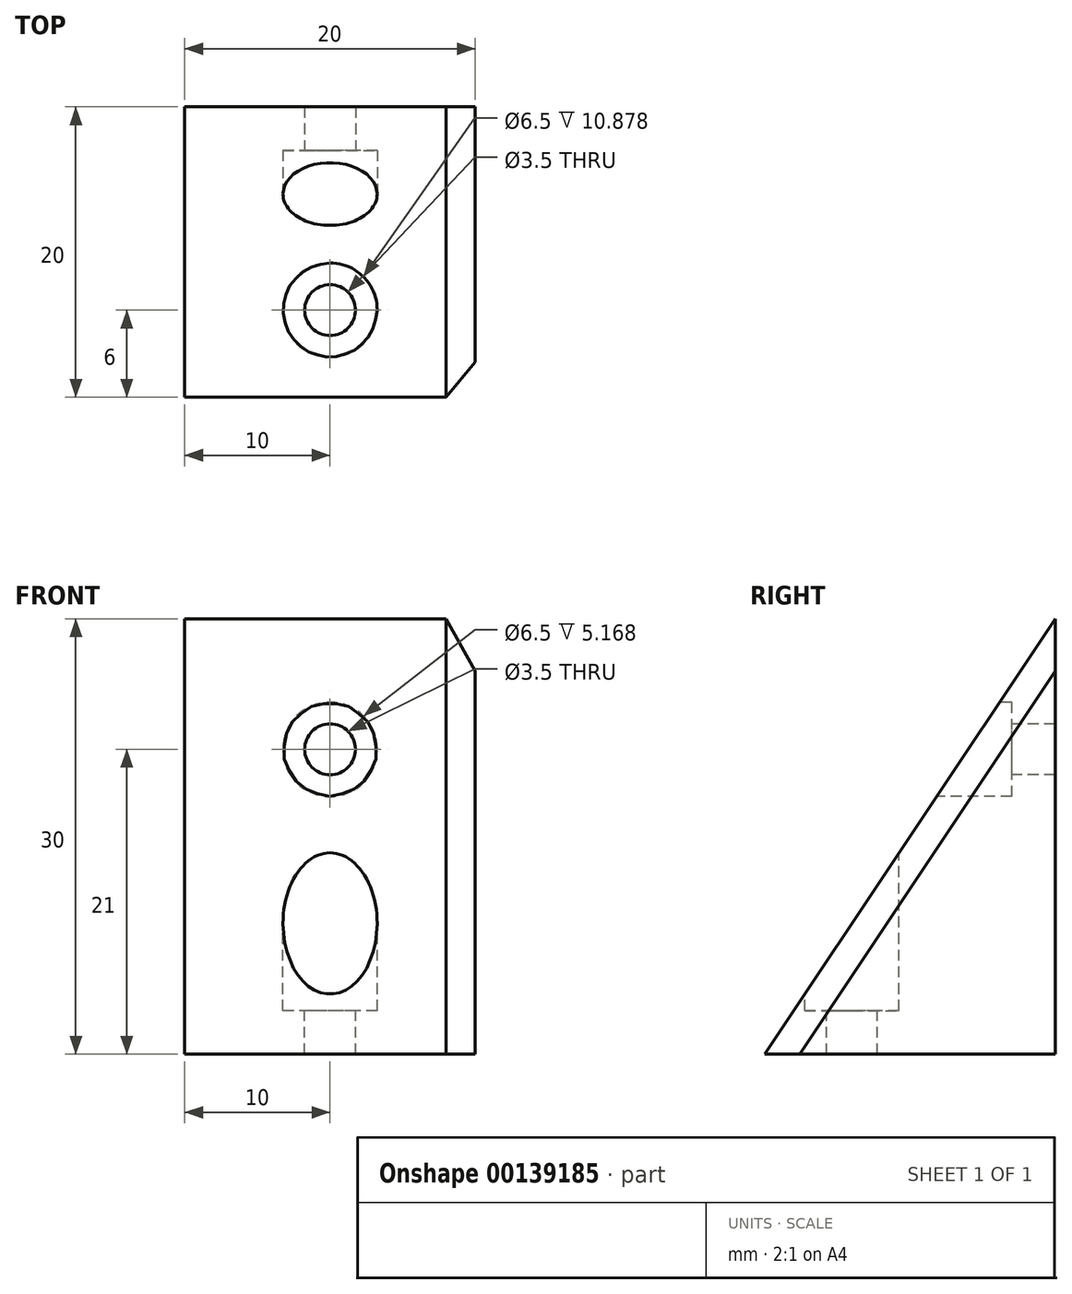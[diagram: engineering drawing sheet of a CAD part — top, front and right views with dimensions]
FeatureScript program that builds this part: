
annotation { "Feature Type Name" : "Feature", "Feature Type Description" : "" }
export const myFeature = defineFeature(function(context is Context, id is Id, definition is map)
    precondition{}
    {
        {
            var Q0;
            Q0=qCreatedBy(makeId("Front.planeOp"),FACE);
            var sketch = newSketch(context, id + "F0", { "sketchPlane" : qUnion([Q0])});
            skLineSegment(sketch, "E0.bottom", {"start": v(0, 0) * mm, "end": v(20, 0) * mm});
            skLineSegment(sketch, "E0.top", {"start": v(0, 30) * mm, "end": v(20, 30) * mm});
            skLineSegment(sketch, "E0.left", {"start": v(0, 0) * mm, "end": v(0, 30) * mm});
            skLineSegment(sketch, "E0.right", {"start": v(20, 0) * mm, "end": v(20, 30) * mm});
            skSolve(sketch);
        }
        {
            var Q0;
            Q0=makeQuery(id+"F0.imprint","IMPRINT",FACE,{"disambiguationData":[TD([[makeQuery(id+"F0.imprint","IMPRINT",EDGE,{"derivedFrom":sQuery(id+"F0.wireOp",EDGE,"E0.bottom")}),1.0]])]});
            extrude(context, id + "F1", {"entities" : qUnion([Q0]), "depth" : 20 * mm});
        }
        {
            var Q0;
            Q0=makeQuery(id+"F1.opExtrude","CAP_FACE",FACE,{"disambiguationData":[OSD([sQuery(id+"F0.wireOp",EDGE,"E0.bottom"),sQuery(id+"F0.wireOp",EDGE,"E0.top"),sQuery(id+"F0.wireOp",EDGE,"E0.left"),sQuery(id+"F0.wireOp",EDGE,"E0.right")])],"isStart":false});
            var sketch = newSketch(context, id + "F2", { "sketchPlane" : qUnion([Q0])});
            skCircle(sketch, "E1", {"center": v(10, 21) * mm, "radius": 3.25 * mm});
            skPoint(sketch, "E1.centerSnap0", {"position": v(10, 30) * mm});
            skCircle(sketch, "E2", {"center": v(10, 21) * mm, "radius": 1.75 * mm});
            skSolve(sketch);
        }
        {
            var Q0;
            Q0=makeQuery(id+"F2.imprint","IMPRINT",FACE,{"disambiguationData":[TD([[makeQuery(id+"F2.imprint","IMPRINT",EDGE,{"derivedFrom":sQuery(id+"F2.wireOp",EDGE,"E1")}),1.0]])]});
            extrude(context, id + "F3", {"entities" : qUnion([Q0]), "operationType" : NewBodyOperationType.REMOVE, "oppositeDirection" : true, "depth" : 17 * mm});
        }
        {
            var Q0;
            Q0=makeQuery(id+"F3.boolean.opBoolean","SPLIT",FACE,{"disambiguationData":[TD([makeQuery(id+"F3.opExtrude","SWEPT_FACE",FACE,{"disambiguationData":[OSD([sQuery(id+"F2.wireOp",EDGE,"E2")])]})])],"derivedFrom":makeQuery(id+"F1.opExtrude","CAP_FACE",FACE,{"disambiguationData":[OSD([sQuery(id+"F0.wireOp",EDGE,"E0.bottom"),sQuery(id+"F0.wireOp",EDGE,"E0.top"),sQuery(id+"F0.wireOp",EDGE,"E0.left"),sQuery(id+"F0.wireOp",EDGE,"E0.right")])],"isStart":false})});
            extrude(context, id + "F4", {"entities" : qUnion([Q0]), "operationType" : NewBodyOperationType.REMOVE, "endBound" : BoundingType.THROUGH_ALL, "oppositeDirection" : true, "depth" : 25 * mm});
        }
        {
            var Q0;
            Q0=makeQuery(id+"F1.opExtrude","SWEPT_FACE",FACE,{"disambiguationData":[OSD([sQuery(id+"F0.wireOp",EDGE,"E0.top")])]});
            var sketch = newSketch(context, id + "F5", { "sketchPlane" : qUnion([Q0])});
            skCircle(sketch, "E3", {"center": v(10, -14) * mm, "radius": 3.25 * mm});
            skPoint(sketch, "E3.centerSnap0", {"position": v(10, 0) * mm});
            skCircle(sketch, "E4", {"center": v(10, -14) * mm, "radius": 1.75 * mm});
            skSolve(sketch);
        }
        {
            var Q0;
            Q0=makeQuery(id+"F1.opExtrude","SWEPT_FACE",FACE,{"disambiguationData":[OSD([sQuery(id+"F0.wireOp",EDGE,"E0.left")])]});
            var sketch = newSketch(context, id + "F6", { "sketchPlane" : qUnion([Q0])});
            skLineSegment(sketch, "E5", {"start": v(0, 30) * mm, "end": v(20, 0) * mm});
            skSolve(sketch);
        }
        {
            var Q0;
            Q0=makeQuery(id+"F6.imprint","IMPRINT",FACE,{"disambiguationData":[TD([[makeQuery(id+"F6.imprint","IMPRINT",EDGE,{"derivedFrom":sQuery(id+"F6.wireOp",EDGE,"E5")}),1.0]])]});
            extrude(context, id + "F7", {"entities" : qUnion([Q0]), "operationType" : NewBodyOperationType.REMOVE, "endBound" : BoundingType.THROUGH_ALL, "oppositeDirection" : true, "depth" : 25 * mm});
        }
        {
            var Q0;
            Q0=makeQuery(id+"F5.imprint","IMPRINT",FACE,{"disambiguationData":[TD([[makeQuery(id+"F5.imprint","IMPRINT",EDGE,{"derivedFrom":sQuery(id+"F5.wireOp",EDGE,"E3")}),1.0]])]});
            extrude(context, id + "F8", {"entities" : qUnion([Q0]), "operationType" : NewBodyOperationType.REMOVE, "oppositeDirection" : true, "depth" : 27 * mm});
        }
        {
            var Q0;
            Q0=makeQuery(id+"F5.imprint","IMPRINT",FACE,{"disambiguationData":[TD([[makeQuery(id+"F5.imprint","IMPRINT",EDGE,{"derivedFrom":sQuery(id+"F5.wireOp",EDGE,"E4")}),1.0]])]});
            extrude(context, id + "F9", {"entities" : qUnion([Q0]), "operationType" : NewBodyOperationType.REMOVE, "endBound" : BoundingType.THROUGH_ALL, "oppositeDirection" : true, "depth" : 25 * mm});
        }
        {
            var Q0;
            Q0=makeQuery(id+"F7.boolean.opBoolean","COPY",EDGE,{"derivedFrom":makeQuery(id+"F7.opExtrude","CAP_EDGE",EDGE,{"disambiguationData":[OSD([sQuery(id+"F6.wireOp",EDGE,"E5")])],"isStart":true})});
            var Q1;
            Q1=makeQuery(id+"F7.boolean.opBoolean","INTERSECT",EDGE,{"derivedFrom":[makeQuery(id+"F1.opExtrude","SWEPT_FACE",FACE,{"disambiguationData":[OSD([sQuery(id+"F0.wireOp",EDGE,"E0.right")])]}),makeQuery(id+"F7.opExtrude","SWEPT_FACE",FACE,{"disambiguationData":[OSD([sQuery(id+"F6.wireOp",EDGE,"E5")])]})]});
            chamfer(context, id + "F10", {"entities" : qUnion([Q0, Q1]), "width" : 2 * mm, "tangentPropagation" : true});
        }
    });
